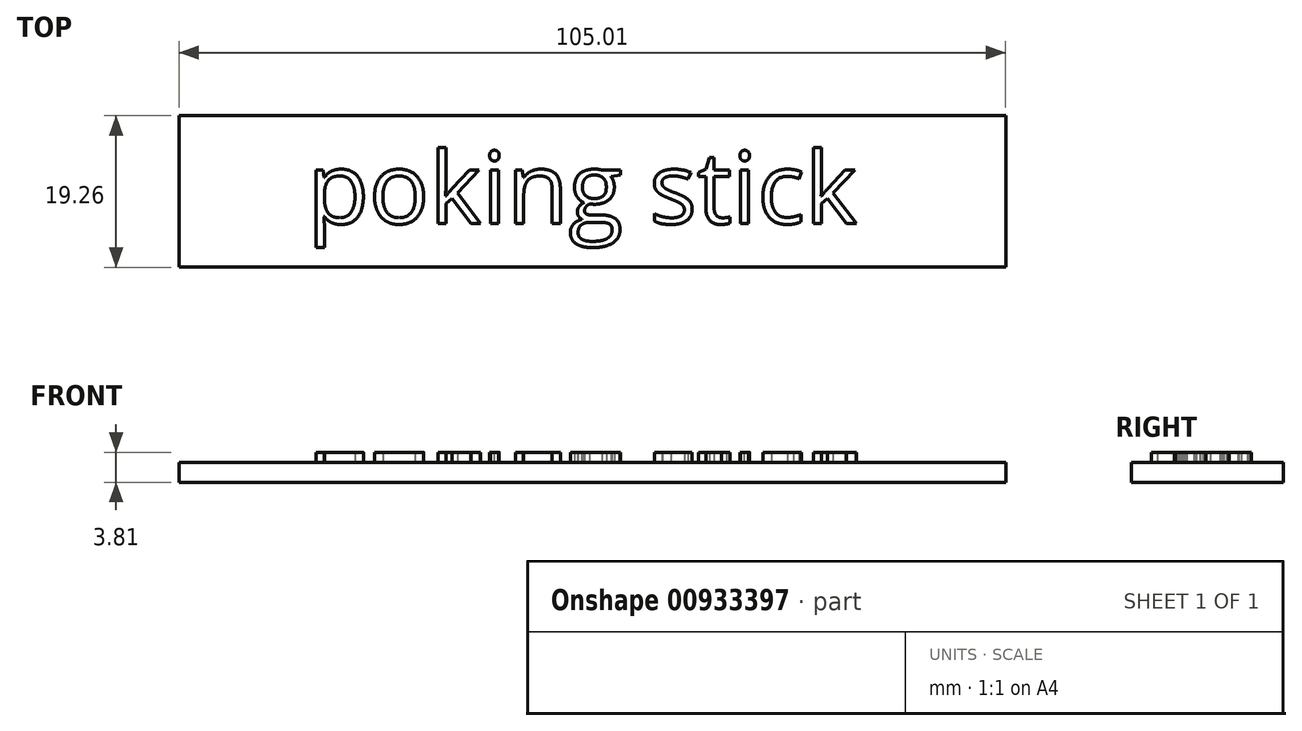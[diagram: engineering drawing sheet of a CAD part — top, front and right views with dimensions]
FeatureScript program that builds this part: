
annotation { "Feature Type Name" : "Feature", "Feature Type Description" : "" }
export const myFeature = defineFeature(function(context is Context, id is Id, definition is map)
    precondition{}
    {
        {
            var Q0;
            Q0=qCreatedBy(makeId("Top.planeOp"),FACE);
            var sketch = newSketch(context, id + "F0", { "sketchPlane" : qUnion([Q0])});
            skLineSegment(sketch, "E0.bottom", {"start": v(-43.5, 9.14) * mm, "end": v(61.51, 9.14) * mm});
            skLineSegment(sketch, "E0.top", {"start": v(-43.5, 28.4) * mm, "end": v(61.51, 28.4) * mm});
            skLineSegment(sketch, "E0.left", {"start": v(-43.5, 9.14) * mm, "end": v(-43.5, 28.4) * mm});
            skLineSegment(sketch, "E0.right", {"start": v(61.51, 9.14) * mm, "end": v(61.51, 28.4) * mm});
            skText(sketch, "E1", { "text": "poking stick", "fontName": "OpenSans-Regular.ttf"});
            const initialGuessF0  = {"E1": [-0.02715, 0.01469, 1, 0, 0.00914]};
            skSetInitialGuess(sketch, initialGuessF0);
            skSolve(sketch);
        }
        {
            var Q0;
            Q0 = qSketchRegion(id + "F0", true);
            var Q1;
            Q1=makeQuery(id+"F0.imprint","IMPRINT",FACE,{"disambiguationData":[TD([[makeQuery(id+"F0.imprint","IMPRINT",EDGE,{"derivedFrom":sQuery(id+"F0.wireOp",EDGE,"E1.sketch_text.stroke-16")}),1.0]])]});
            var Q2;
            Q2=makeQuery(id+"F0.imprint","IMPRINT",FACE,{"disambiguationData":[TD([[makeQuery(id+"F0.imprint","IMPRINT",EDGE,{"derivedFrom":sQuery(id+"F0.wireOp",EDGE,"E1.sketch_text.stroke-34")}),1.0]])]});
            var Q3;
            Q3=makeQuery(id+"F0.imprint","IMPRINT",FACE,{"disambiguationData":[TD([[makeQuery(id+"F0.imprint","IMPRINT",EDGE,{"derivedFrom":sQuery(id+"F0.wireOp",EDGE,"E1.sketch_text.stroke-124")}),1.0]])]});
            var Q4;
            Q4=makeQuery(id+"F0.imprint","IMPRINT",FACE,{"disambiguationData":[TD([[makeQuery(id+"F0.imprint","IMPRINT",EDGE,{"derivedFrom":sQuery(id+"F0.wireOp",EDGE,"E1.sketch_text.stroke-115")}),1.0]])]});
            extrude(context, id + "F1", {"entities" : qUnion([Q0, Q1, Q2, Q3, Q4]), "depth" : 2.54 * mm, "offsetDistance" : 25.4 * mm});
        }
        {
            var Q0;
            Q0=makeQuery(id+"F0.imprint","IMPRINT",FACE,{"disambiguationData":[TD([[makeQuery(id+"F0.imprint","IMPRINT",EDGE,{"derivedFrom":sQuery(id+"F0.wireOp",EDGE,"E1.sketch_text.stroke-0")}),-1.0]])]});
            var Q1;
            Q1=makeQuery(id+"F0.imprint","IMPRINT",FACE,{"disambiguationData":[TD([[makeQuery(id+"F0.imprint","IMPRINT",EDGE,{"derivedFrom":sQuery(id+"F0.wireOp",EDGE,"E1.sketch_text.stroke-25")}),-1.0]])]});
            var Q2;
            Q2=makeQuery(id+"F0.imprint","IMPRINT",FACE,{"disambiguationData":[TD([[makeQuery(id+"F0.imprint","IMPRINT",EDGE,{"derivedFrom":sQuery(id+"F0.wireOp",EDGE,"E1.sketch_text.stroke-42")}),-1.0]])]});
            var Q3;
            Q3=makeQuery(id+"F0.imprint","IMPRINT",FACE,{"disambiguationData":[TD([[makeQuery(id+"F0.imprint","IMPRINT",EDGE,{"derivedFrom":sQuery(id+"F0.wireOp",EDGE,"E1.sketch_text.stroke-57")}),-1.0]])]});
            var Q4;
            Q4=makeQuery(id+"F0.imprint","IMPRINT",FACE,{"disambiguationData":[TD([[makeQuery(id+"F0.imprint","IMPRINT",EDGE,{"derivedFrom":sQuery(id+"F0.wireOp",EDGE,"E1.sketch_text.stroke-61")}),-1.0]])]});
            var Q5;
            Q5=makeQuery(id+"F0.imprint","IMPRINT",FACE,{"disambiguationData":[TD([[makeQuery(id+"F0.imprint","IMPRINT",EDGE,{"derivedFrom":sQuery(id+"F0.wireOp",EDGE,"E1.sketch_text.stroke-69")}),-1.0]])]});
            var Q6;
            Q6=makeQuery(id+"F0.imprint","IMPRINT",FACE,{"disambiguationData":[TD([[makeQuery(id+"F0.imprint","IMPRINT",EDGE,{"derivedFrom":sQuery(id+"F0.wireOp",EDGE,"E1.sketch_text.stroke-86")}),-1.0]])]});
            var Q7;
            Q7=makeQuery(id+"F0.imprint","IMPRINT",FACE,{"disambiguationData":[TD([[makeQuery(id+"F0.imprint","IMPRINT",EDGE,{"derivedFrom":sQuery(id+"F0.wireOp",EDGE,"E1.sketch_text.stroke-130")}),-1.0]])]});
            var Q8;
            Q8=makeQuery(id+"F0.imprint","IMPRINT",FACE,{"disambiguationData":[TD([[makeQuery(id+"F0.imprint","IMPRINT",EDGE,{"derivedFrom":sQuery(id+"F0.wireOp",EDGE,"E1.sketch_text.stroke-155")}),-1.0]])]});
            var Q9;
            Q9=makeQuery(id+"F0.imprint","IMPRINT",FACE,{"disambiguationData":[TD([[makeQuery(id+"F0.imprint","IMPRINT",EDGE,{"derivedFrom":sQuery(id+"F0.wireOp",EDGE,"E1.sketch_text.stroke-174")}),-1.0]])]});
            var Q10;
            Q10=makeQuery(id+"F0.imprint","IMPRINT",FACE,{"disambiguationData":[TD([[makeQuery(id+"F0.imprint","IMPRINT",EDGE,{"derivedFrom":sQuery(id+"F0.wireOp",EDGE,"E1.sketch_text.stroke-178")}),-1.0]])]});
            var Q11;
            Q11=makeQuery(id+"F0.imprint","IMPRINT",FACE,{"disambiguationData":[TD([[makeQuery(id+"F0.imprint","IMPRINT",EDGE,{"derivedFrom":sQuery(id+"F0.wireOp",EDGE,"E1.sketch_text.stroke-186")}),-1.0]])]});
            var Q12;
            Q12=makeQuery(id+"F0.imprint","IMPRINT",FACE,{"disambiguationData":[TD([[makeQuery(id+"F0.imprint","IMPRINT",EDGE,{"derivedFrom":sQuery(id+"F0.wireOp",EDGE,"E1.sketch_text.stroke-201")}),-1.0]])]});
            extrude(context, id + "F2", {"entities" : qUnion([Q0, Q1, Q2, Q3, Q4, Q5, Q6, Q7, Q8, Q9, Q10, Q11, Q12]), "operationType" : NewBodyOperationType.ADD, "depth" : 3.8 * mm, "offsetDistance" : 25.4 * mm});
        }
    });
